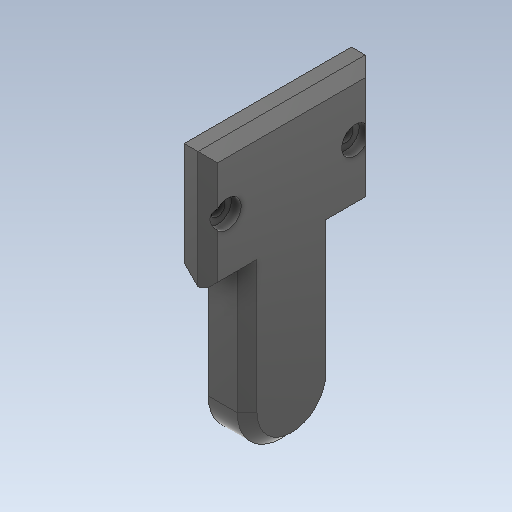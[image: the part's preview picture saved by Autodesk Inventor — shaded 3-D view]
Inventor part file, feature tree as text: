
AUTODESK INVENTOR PART (.ipt)
format: ipt  version: 2020 (Build 240168000, 168)  size: 506,880 bytes
history: native  units: mm
features: extrude x20, sketch x18, reference x8, projected_geometry x7, other x6, chamfer x5, plane x2, hole x1, mirror x1, delete_face x1
ambient origin geometry x8: Origin, YZ Plane, XZ Plane, XY Plane, X Axis, Y Axis, Z Axis, Center Point
bodies: Solid1 (feature_tree), Solid2 (feature_tree)
feature tree (69):
  extrude  "Extrusion1"  Depth=18.0mm
  plane  "Work Plane1"
  extrude  "Extrusion2"  Depth=18.0mm
  extrude  "Extrusion3"  Depth=2.0mm TaperAngle=0.0deg
  extrude  "Extrusion4"  TaperAngle=0.0deg  [1 undecoded]
  extrude  "Extrusion5"  Depth=50.1mm TaperAngle=0.0deg
  sketch  "Sketch6"  dims[d14=7.199887mm d15=3.599976mm]
  extrude  "Extrusion6"  Depth=3.599976mm
  extrude  "Extrusion7"  Depth=0.15mm
  extrude  "Extrusion8"  Depth=0.15mm
  extrude  "Extrusion10"  Depth=15.9mm TaperAngle=0.0deg
  extrude  "Extrusion11"  Depth=6.5mm
  extrude  "Extrusion12"  Depth=3.925mm
  extrude  "Extrusion13"  Depth=5.15mm
  sketch  "Sketch14"  dims[d29=2.525mm d30=5.15mm]
  extrude  "Extrusion14"  Depth=12.55mm
  extrude  "Extrusion15"  Depth=2.75mm TaperAngle=0.0deg
  hole  "Hole1"  [1 undecoded]
  extrude  "Extrusion16"  Depth=2.525mm
  plane  "Work Plane2"
  mirror  "Mirror1"
  delete_face  "Delete Face2"
  extrude  "Extrusion18"  Depth=23.15mm
  extrude  "Extrusion19"  Depth=10.0mm
  extrude  "Extrusion20"  TaperAngle=0.0deg  [1 undecoded]
  extrude  "Extrusion21"  Depth=2.0mm
  chamfer  "Chamfer1"  Distance=19.0mm
  chamfer  "Chamfer2"  [1 undecoded]
  chamfer  "Chamfer3"  Distance=8.8mm
  extrude  "Extrusion22"  Depth=2.0mm
  chamfer  "Chamfer4"  Distance=2.525mm
  chamfer  "Chamfer5"  Distance=23.15mm
  sketch  "Sketch1"  dims[d0=18.0mm d1=45.0mm]
  reference  "Reference1"
  sketch  "Sketch2"  dims[d2=45.0mm d3=18.0mm]
  reference  "Reference2"
  sketch  "Sketch3"  dims[d4=18.0mm d5=51.1mm d6=2.0mm d7=0.0mm d8=0.0mm]
  reference  "Reference3"
  reference  "Reference4"
  reference  "Reference5"
  reference  "Reference6"
  reference  "Reference7"
  reference  "Reference8"
  sketch  "Sketch4"  dims[d9=37.3mm d10=0.0mm]
  sketch  "Sketch5"  dims[d11=35.0mm d12=50.1mm d13=0.0mm]
  sketch  "Sketch8"  dims[d16=0.15mm d17=0.15mm]
  sketch  "Sketch10"  dims[d18=0.15mm d19=0.15mm]
  sketch  "Sketch11"  dims[d20=5.4mm d21=0.0mm d22=15.9mm d23=0.0mm]
  sketch  "Sketch12"  dims[d24=6.5mm d25=0.0mm d26=23.15mm]
  sketch  "Sketch13"  dims[d27=12.55mm d28=3.925mm]
  sketch  "Sketch15"  dims[d31=5.15mm d32=12.55mm]
  sketch  "Sketch17"  dims[d33=40.75mm d34=0.0mm d35=2.75mm d36=0.0mm]
  other  "Pattern of Solid1:1"
  sketch  "Sketch19"  dims[d43=11.85mm d44=23.15mm]
  projected_geometry  "Projected Loop1"
  sketch  "Sketch20"  dims[d45=3.925mm d46=2.525mm]
  projected_geometry  "Projected Loop2"
  sketch  "Sketch21"  dims[d47=12.55mm d48=23.15mm]
  projected_geometry  "Projected Loop3"
  projected_geometry  "Projected Loop4"
  projected_geometry  "Projected Loop5"
  projected_geometry  "Projected Loop6"
  sketch  "Sketch23"  dims[d49=10.05mm d50=0.0mm d54=10.0mm d55=0.0mm d56=0.0mm d57=19.0mm d58=0.0mm d59=8.8mm d60=5.925mm d61=2.525mm d62=23.15mm d63=15.075mm d64=23.15mm d65=6.05mm d66=23.15mm d67=12.55mm d68=0.0mm d72=8.8mm d73=10.0mm d74=10.2mm d75=17.225mm d76=4.0mm d77=0.0mm d78=3.85mm d79=10.925mm d80=5.0mm d81=0.0mm d82=0.765mm d83=1.0mm d84=0.0mm d85=18.0mm d86=5.0mm d87=5.0mm d88=53.1mm d89=0.0mm d90=53.1mm d91=0.0mm d92=3.0mm d93=6.0mm d94=4.0mm d95=2.0mm d96=90.0deg d97=40.0mm d98=0.0mm d99=3.1mm d100=2.4mm d101=0.0mm d105=3.1mm d106=2.4mm d107=0.0mm d108=8.0mm d109=8.0mm d110=24.0mm d111=3.0mm d112=3.0mm d113=26.0mm d114=4.0mm d115=4.0mm d116=12.0mm d117=10.0mm d118=0.0mm d119=3.1mm d120=3.1mm d121=2.4mm d122=0.0mm d123=51.141786mm d124=30.859708mm d125=100.0mm d126=0.0mm d127=3.0mm d128=2.0mm d129=45.0deg d130=0.01mm d131=2.0mm d132=45.0deg d133=3.0mm d134=2.0mm d135=45.0deg d136=5.6mm d137=5.6mm d138=2.0mm d139=0.0mm d140=2.0mm d141=2.0mm d142=45.0deg d143=1.0mm d144=2.0mm d145=45.0deg]
  projected_geometry  "Projected Loop7"
  parser-record x1  (decoder bookkeeping rows leaked as tree rows — omitted from the tree; the rows remain in map.json)
  other  "Demo2.0004.iam"
  other  "Bearing:2"
  other  "Rolling bearing GB/T 7218-1995 Type FSN 70000-Z F 623-Z:1"
  other  "servo horn 1:1"
note: 4 required parameter values undecoded (feature->parameter linkage not recoverable at this tier; creation-order binding heuristic only, values carry confidence <= 0.55)
note: 1 file-system path scrubbed to <path> (originals preserved in map.json)
